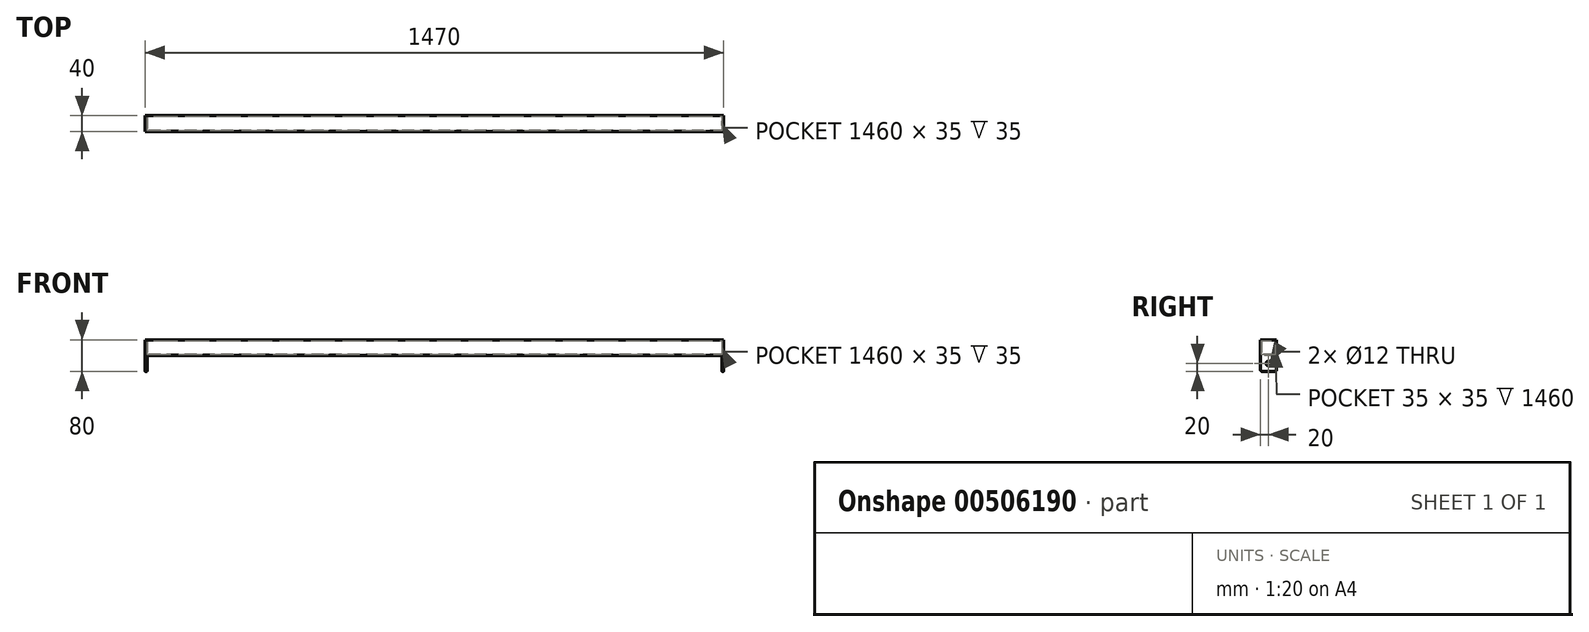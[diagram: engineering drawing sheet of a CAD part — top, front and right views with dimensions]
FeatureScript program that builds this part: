
annotation { "Feature Type Name" : "Feature", "Feature Type Description" : "" }
export const myFeature = defineFeature(function(context is Context, id is Id, definition is map)
    precondition{}
    {
        {
            var Q0;
            Q0=qCreatedBy(makeId("Right.planeOp"),FACE);
            var sketch = newSketch(context, id + "F0", { "sketchPlane" : qUnion([Q0])});
            skLineSegment(sketch, "E0.bottom", {"start": v(20, 20) * mm, "end": v(-20, 20) * mm});
            skLineSegment(sketch, "E0.top", {"start": v(20, -20) * mm, "end": v(-20, -20) * mm});
            skLineSegment(sketch, "E0.left", {"start": v(20, 20) * mm, "end": v(20, -20) * mm});
            skLineSegment(sketch, "E0.right", {"start": v(-20, 20) * mm, "end": v(-20, -20) * mm});
            skPoint(sketch, "E0.middle", {"position": v(0, 0) * mm});
            skLineSegment(sketch, "E1.bottom", {"start": v(17.5, 17.5) * mm, "end": v(-17.5, 17.5) * mm});
            skLineSegment(sketch, "E1.top", {"start": v(17.5, -17.5) * mm, "end": v(-17.5, -17.5) * mm});
            skLineSegment(sketch, "E1.left", {"start": v(17.5, 17.5) * mm, "end": v(17.5, -17.5) * mm});
            skLineSegment(sketch, "E1.right", {"start": v(-17.5, 17.5) * mm, "end": v(-17.5, -17.5) * mm});
            skSolve(sketch);
        }
        {
            var Q0;
            Q0=makeQuery(id+"F0.imprint","IMPRINT",FACE,{"disambiguationData":[TD([[makeQuery(id+"F0.imprint","IMPRINT",EDGE,{"derivedFrom":sQuery(id+"F0.wireOp",EDGE,"E0.bottom")}),1.0]])]});
            extrude(context, id + "F1", {"entities" : qUnion([Q0]), "endBound" : BoundingType.SYMMETRIC, "depth" : 1460 * mm});
        }
        {
            var Q0;
            Q0=makeQuery(id+"F1.opExtrude","CAP_FACE",FACE,{"disambiguationData":[OSD([sQuery(id+"F0.wireOp",EDGE,"E0.bottom"),sQuery(id+"F0.wireOp",EDGE,"E0.top"),sQuery(id+"F0.wireOp",EDGE,"E0.left"),sQuery(id+"F0.wireOp",EDGE,"E0.right"),sQuery(id+"F0.wireOp",EDGE,"E1.bottom"),sQuery(id+"F0.wireOp",EDGE,"E1.top"),sQuery(id+"F0.wireOp",EDGE,"E1.left"),sQuery(id+"F0.wireOp",EDGE,"E1.right")])],"isStart":false});
            var sketch = newSketch(context, id + "F2", { "sketchPlane" : qUnion([Q0])});
            skLineSegment(sketch, "E2.bottom", {"start": v(20, 20) * mm, "end": v(-20, 20) * mm});
            skLineSegment(sketch, "E2.top", {"start": v(17, -60) * mm, "end": v(-17, -60) * mm});
            skLineSegment(sketch, "E2.left", {"start": v(20, 20) * mm, "end": v(20, -57) * mm});
            skLineSegment(sketch, "E2.right", {"start": v(-20, 20) * mm, "end": v(-20, -57) * mm});
            skLineSegment(sketch, "E3.left", {"start": v(20, 20) * mm, "end": v(20, -20) * mm});
            skCircle(sketch, "E4", {"center": v(0, -40) * mm, "radius": 6 * mm});
            skPoint(sketch, "E4.centerSnap0", {"position": v(0, -60) * mm});
            skPoint(sketch, "E5.visualSharp", {"position": v(-20, -60) * mm});
            skArc(sketch, "E5.filletArc", {"start": v(-20, -57) * mm, "mid": v(-19.12, -59.12) * mm, "end": v(-17, -60) * mm});
            skPoint(sketch, "E6.visualSharp", {"position": v(20, -60) * mm});
            skArc(sketch, "E6.filletArc", {"start": v(17, -60) * mm, "mid": v(19.12, -59.12) * mm, "end": v(20, -57) * mm});
            skSolve(sketch);
        }
        {
            var Q0;
            Q0=qSketchRegion(id+"F2",true);
            extrude(context, id + "F3", {"entities" : qUnion([Q0]), "depth" : 5 * mm});
        }
        {
            var Q0;
            Q0=makeQuery(id+"F3.opExtrude","SWEPT_BODY",BODY,{"disambiguationData":[OSD([sQuery(id+"F2.wireOp",EDGE,"E2.top"),sQuery(id+"F2.wireOp",EDGE,"E2.left"),sQuery(id+"F2.wireOp",EDGE,"E2.right"),sQuery(id+"F2.wireOp",EDGE,"E3.bottom"),sQuery(id+"F2.wireOp",EDGE,"E3.top"),sQuery(id+"F2.wireOp",EDGE,"E3.left"),sQuery(id+"F2.wireOp",EDGE,"E3.right"),sQuery(id+"F2.wireOp",EDGE,"gTgGaeDv-OfJh-3z9d-mSEW-kqISW2qM0Zl8"),sQuery(id+"F2.wireOp",EDGE,"E4"),sQuery(id+"F2.wireOp",EDGE,"d7060350-439c-4211-ad83-2698a1f480e9.filletArc"),sQuery(id+"F2.wireOp",EDGE,"1f8af891-f8d6-47e9-a65d-fee356d0fddc.filletArc"),sQuery(id+"F2.wireOp",EDGE,"E5.filletArc"),sQuery(id+"F2.wireOp",EDGE,"E6.filletArc")])]});
            var Q1;
            Q1=qCreatedBy(makeId("Right.planeOp"),FACE);
            mirror(context, id + "F4", {"operationType" : NewBodyOperationType.ADD, "entities" : qUnion([Q0]), "mirrorPlane" : qUnion([Q1])});
        }
    });
